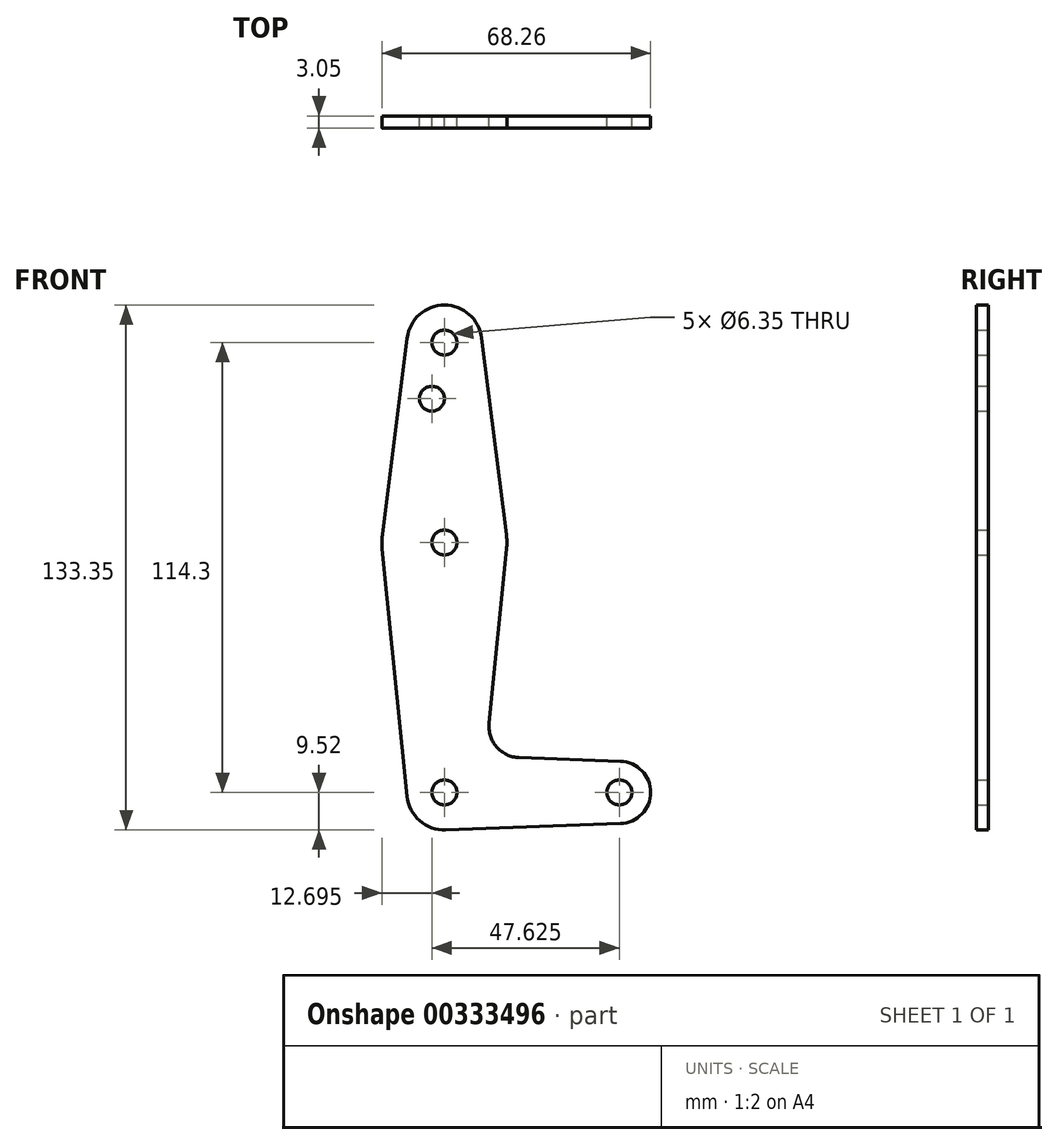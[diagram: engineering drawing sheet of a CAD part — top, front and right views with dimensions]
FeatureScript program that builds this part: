
annotation { "Feature Type Name" : "Feature", "Feature Type Description" : "" }
export const myFeature = defineFeature(function(context is Context, id is Id, definition is map)
    precondition{}
    {
        {
            var Q0;
            Q0=qCreatedBy(makeId("Front.planeOp"),FACE);
            var sketch = newSketch(context, id + "F0", { "sketchPlane" : qUnion([Q0])});
            skLineSegment(sketch, "E0", {"start": v(0, 0) * mm, "end": v(0, 114.3) * mm, "construction": true});
            skLineSegment(sketch, "E1", {"start": v(0, 0) * mm, "end": v(44.45, 0) * mm, "construction": true});
            skCircle(sketch, "E2", {"center": v(0, 0) * mm, "radius": 9.53 * mm});
            skCircle(sketch, "E3", {"center": v(44.45, 0) * mm, "radius": 7.94 * mm});
            skCircle(sketch, "E4", {"center": v(0, 114.3) * mm, "radius": 9.53 * mm});
            skCircle(sketch, "E5", {"center": v(0, 63.5) * mm, "radius": 15.88 * mm});
            skLineSegment(sketch, "E6", {"start": v(-15.75, 65.48) * mm, "end": v(-9.45, 115.5) * mm});
            skLineSegment(sketch, "E7", {"start": v(15.75, 65.48) * mm, "end": v(9.45, 115.5) * mm});
            skLineSegment(sketch, "E8", {"start": v(11.34, 17.6) * mm, "end": v(15.8, 61.91) * mm});
            skLineSegment(sketch, "E9", {"start": v(-9.48, -0.95) * mm, "end": v(-15.8, 61.91) * mm});
            skLineSegment(sketch, "E10", {"start": v(0.34, -9.52) * mm, "end": v(44.73, -7.93) * mm});
            skLineSegment(sketch, "E11", {"start": v(18.97, 8.85) * mm, "end": v(44.73, 7.93) * mm});
            skCircle(sketch, "E12", {"center": v(0, 114.3) * mm, "radius": 3.18 * mm});
            skCircle(sketch, "E13", {"center": v(0, 63.5) * mm, "radius": 3.18 * mm});
            skCircle(sketch, "E14", {"center": v(0, 0) * mm, "radius": 3.18 * mm});
            skCircle(sketch, "E15", {"center": v(44.45, 0) * mm, "radius": 3.18 * mm});
            skCircle(sketch, "E16", {"center": v(-3.18, 100.03) * mm, "radius": 3.18 * mm});
            skArc(sketch, "E17.filletArc", {"start": v(11.34, 17.6) * mm, "mid": v(13.26, 11.57) * mm, "end": v(18.97, 8.85) * mm});
            skSolve(sketch);
        }
        {
            var Q0;
            Q0 = qSketchRegion(id + "F0", true);
            var Q1;
            Q1 = qSketchRegion(id + "F2", true);
            extrude(context, id + "F1", {"entities" : qUnion([Q0, Q1]), "depth" : 3.05 * mm});
        }
    });
